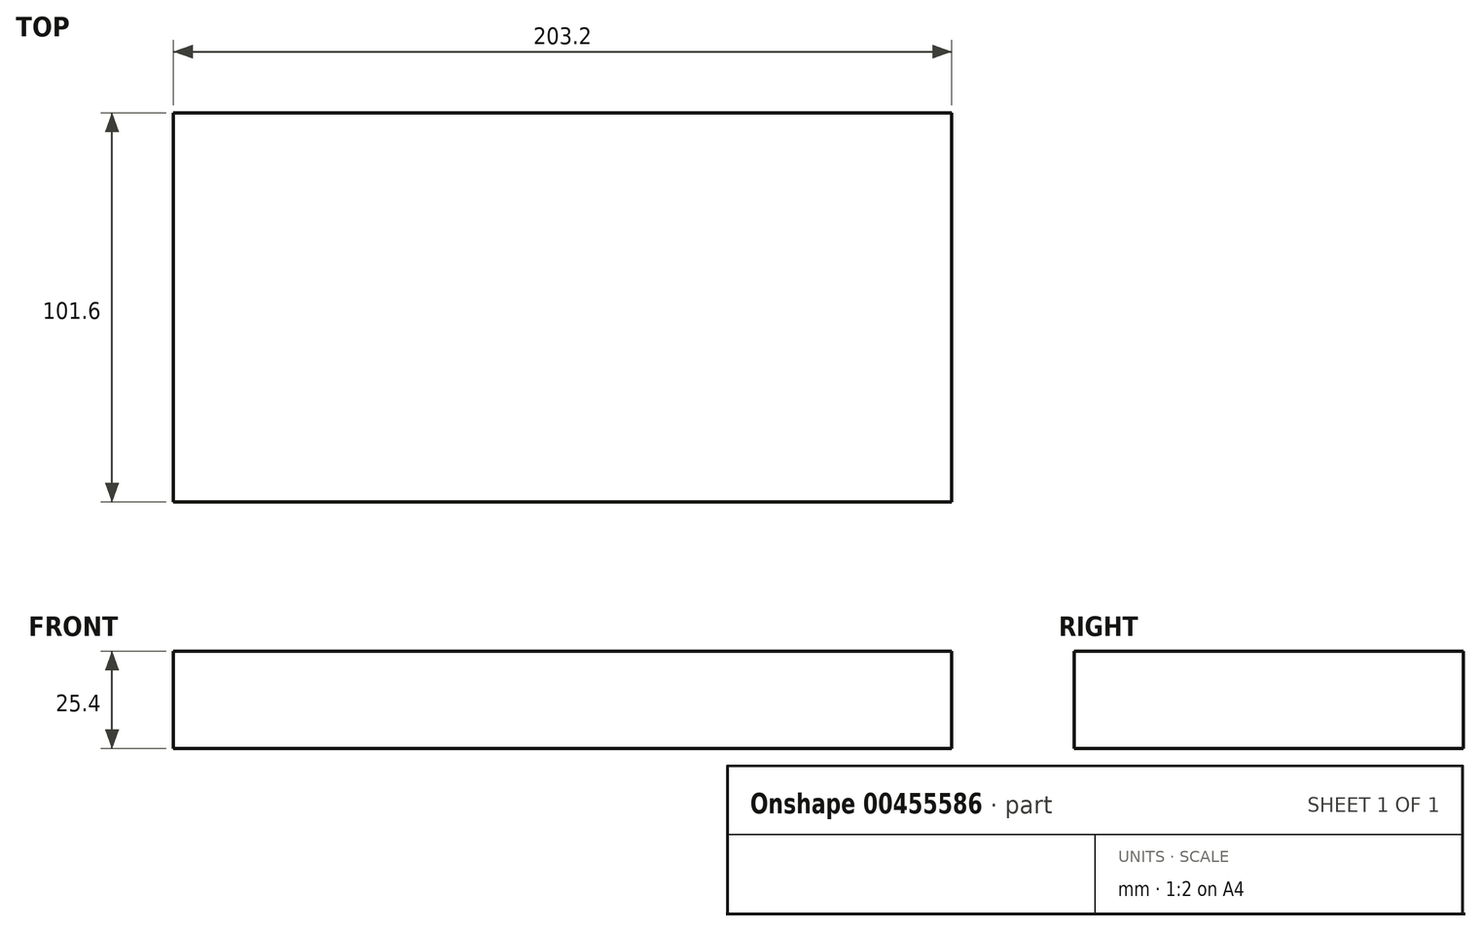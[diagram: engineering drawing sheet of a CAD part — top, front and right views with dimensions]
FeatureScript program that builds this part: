
annotation { "Feature Type Name" : "Feature", "Feature Type Description" : "" }
export const myFeature = defineFeature(function(context is Context, id is Id, definition is map)
    precondition{}
    {
        {
            var Q0;
            Q0=qCreatedBy(makeId("Top.planeOp"),FACE);
            var sketch = newSketch(context, id + "F0", { "sketchPlane" : qUnion([Q0])});
            skLineSegment(sketch, "E0.bottom", {"start": v(101.6, 53.45) * mm, "end": v(-101.6, 53.45) * mm});
            skLineSegment(sketch, "E0.top", {"start": v(101.6, -48.15) * mm, "end": v(-101.6, -48.15) * mm});
            skLineSegment(sketch, "E0.left", {"start": v(101.6, 53.45) * mm, "end": v(101.6, -48.15) * mm});
            skLineSegment(sketch, "E0.right", {"start": v(-101.6, 53.45) * mm, "end": v(-101.6, -48.15) * mm});
            skPoint(sketch, "E0.middle", {"position": v(0, 2.65) * mm});
            skSolve(sketch);
        }
        {
            var Q0;
            Q0 = qSketchRegion(id + "F0", true);
            extrude(context, id + "F1", {"entities" : qUnion([Q0]), "depth" : 25.4 * mm});
        }
    });
